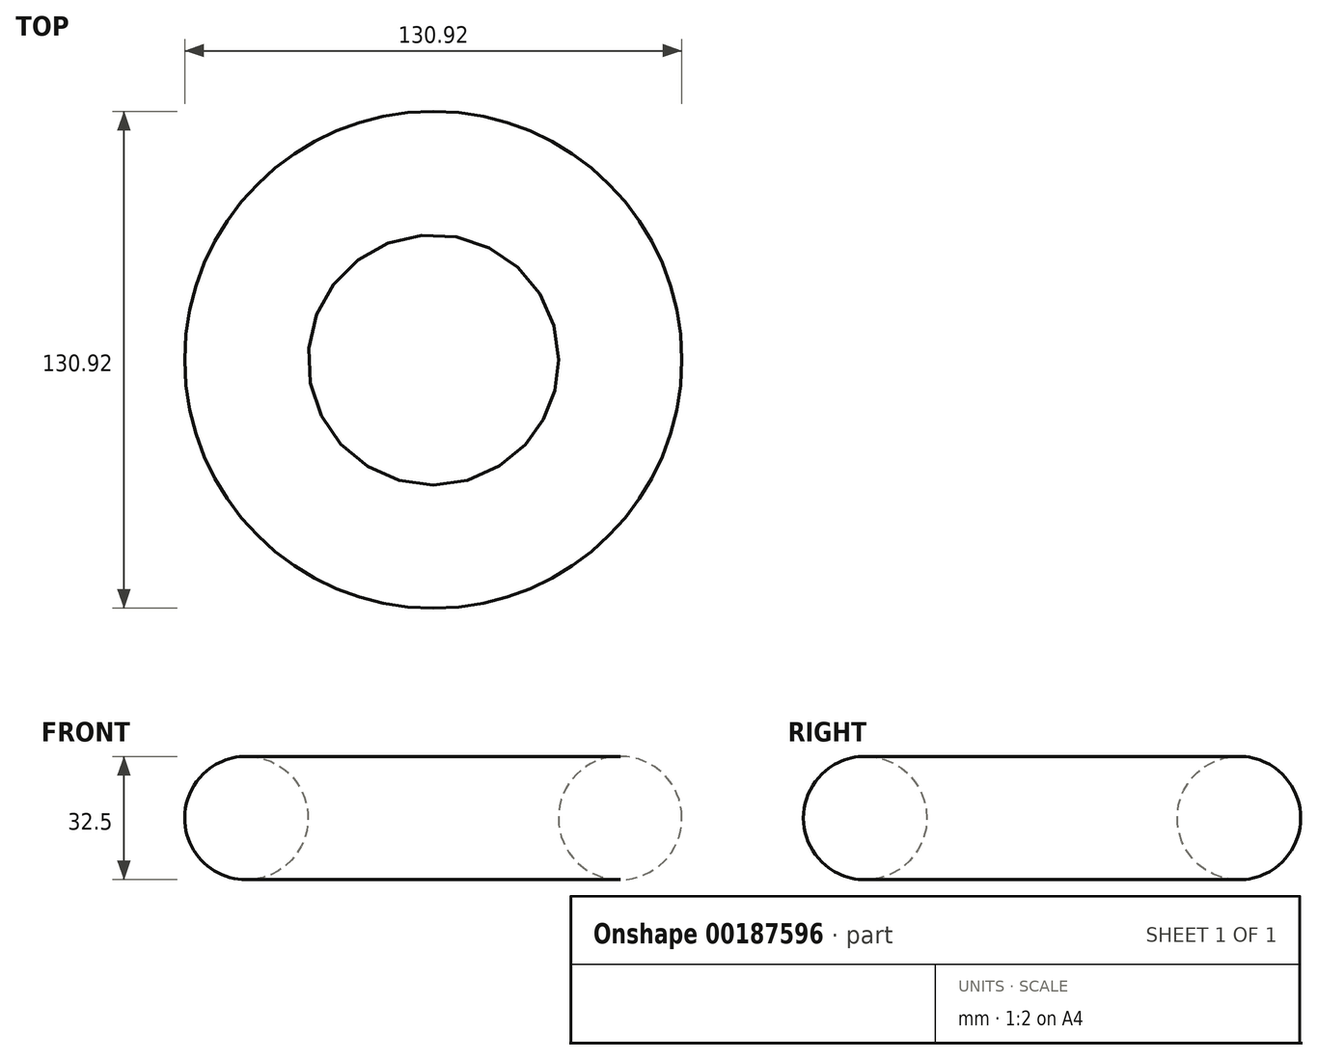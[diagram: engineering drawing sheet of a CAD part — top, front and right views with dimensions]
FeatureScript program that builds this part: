
annotation { "Feature Type Name" : "Feature", "Feature Type Description" : "" }
export const myFeature = defineFeature(function(context is Context, id is Id, definition is map)
    precondition{}
    {
        {
            var Q0;
            Q0=qCreatedBy(makeId("Front.planeOp"),FACE);
            var sketch = newSketch(context, id + "F0", { "sketchPlane" : qUnion([Q0])});
            skCircle(sketch, "E0", {"center": v(49.2, -5.14) * mm, "radius": 16.25 * mm});
            skLineSegment(sketch, "E1", {"start": v(0, 16.76) * mm, "end": v(0, -19.38) * mm});
            skSolve(sketch);
        }
        {
            var Q0;
            Q0=makeQuery(id+"F0.imprint","IMPRINT",FACE,{"disambiguationData":[TD([[makeQuery(id+"F0.imprint","IMPRINT",EDGE,{"derivedFrom":sQuery(id+"F0.wireOp",EDGE,"E0")}),1.0]])]});
            var Q1;
            Q1=sQuery(id+"F0.wireOp",EDGE,"E1");
            revolve(context, id + "F1", {"entities" : qUnion([Q0]), "axis" : qUnion([Q1]), "revolveType" : RevolveType.FULL});
        }
    });
